# Revit family: E-Smart Boiler 50
name_source: partatom
category: Generic Models
revit_build: Autodesk Revit 2018 (Build: 20170223_1515(x64)
units: mm (PartAtom-declared; Revit-internal decimal feet)

## family parameters
Always vertical = Yes
Can host rebar = No
Cut with Voids When Loaded = No
Part Type = Normal
Room Calculation Point = No
Round Connector Dimension = Use Diameter
Shared = No
Work Plane-Based = No

## types (1)
- E-Smart Boiler 50
    Boiler = Coating wit
    Hoogte = 553 mm  [stored 1.8143 ft]
    Hoogte beugel = 224 mm
    Kunststof 1 = Kunststof grijs
    Kunststof 2 = Kunststof zwart
    Kunststof 3 = Kunststof grijs mat
    Kunststof 4 = Kunststof zwart mat
    Kunststof 5 = Kunststof blauw
    Kunststof 6 = Kunststof rood
    Kunststof 7 = Kunststof wit mat
    Scherm = Scherm

note: [stored X ft] marks values corroborated as IEEE doubles in the binary element streams (Revit-internal decimal feet)

## geometry (parser evidence)
native form markers: Sweep x5
no freeform markers — native parametric forms only
